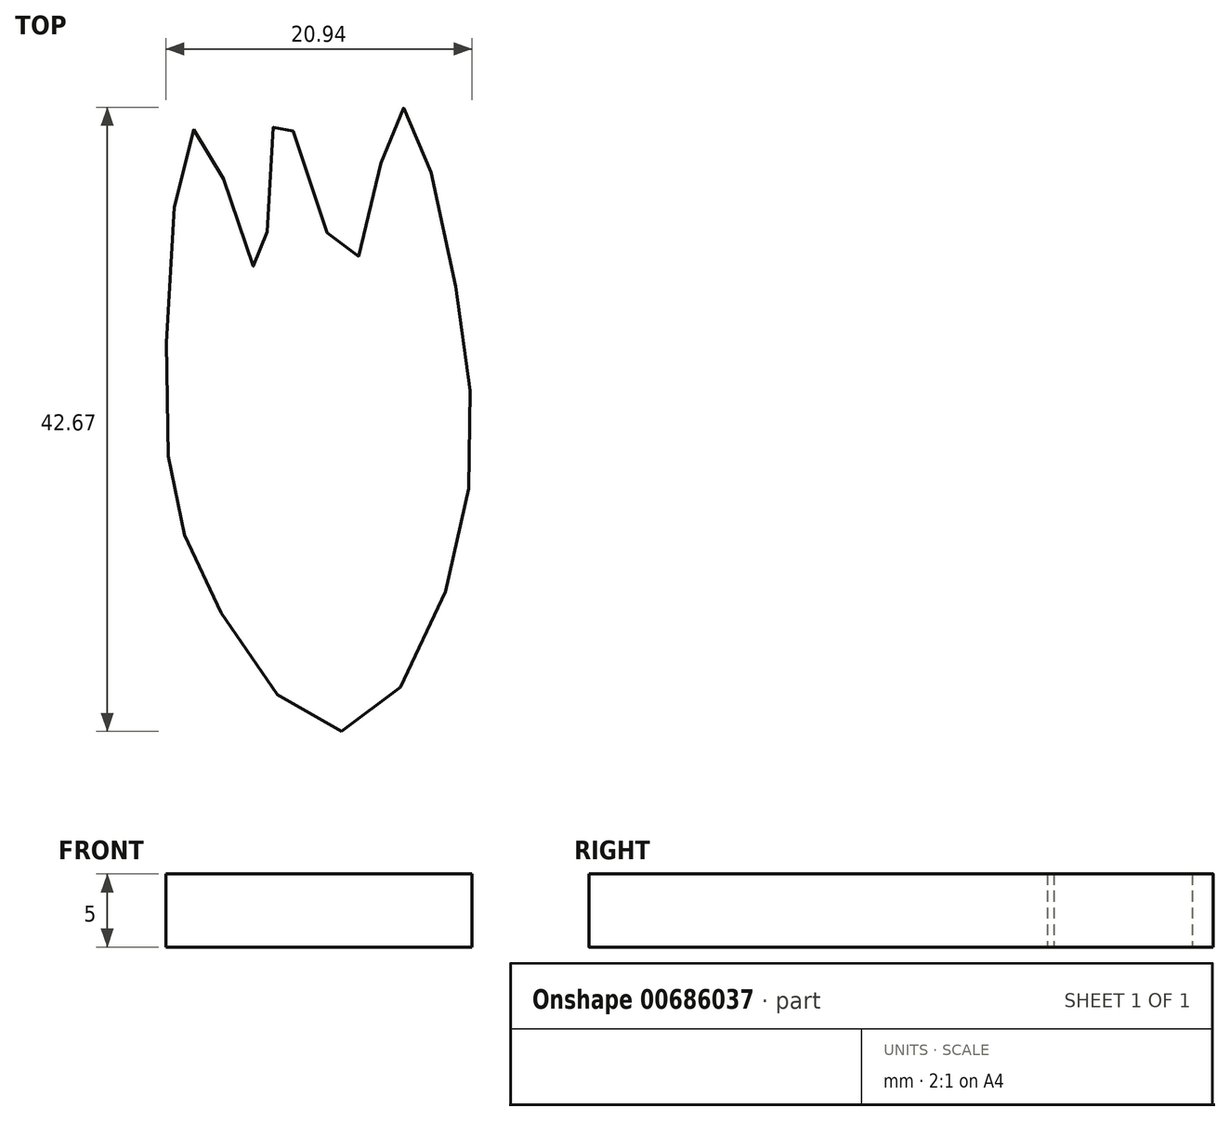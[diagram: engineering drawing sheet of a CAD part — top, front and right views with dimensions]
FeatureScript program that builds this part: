
annotation { "Feature Type Name" : "Feature", "Feature Type Description" : "" }
export const myFeature = defineFeature(function(context is Context, id is Id, definition is map)
    precondition{}
    {
        {
            var Q0;
            Q0=qCreatedBy(makeId("Top.planeOp"),FACE);
            var sketch = newSketch(context, id + "F0", { "sketchPlane" : qUnion([Q0])});
            skFitSpline(sketch, "E0", {"points": [v(31.23, -50.34) * mm, v(22.11, -40.56) * mm, v(19.22, -27) * mm, v(21.67, -9.22) * mm, v(25.67, -19) * mm, v(27, -7.67) * mm, v(31.67, -18.56) * mm, v(35, -7.89) * mm, v(38.78, -18.56) * mm, v(39.23, -37.67) * mm, v(31.23, -50.34) * mm]});
            skFitSpline(sketch, "E1", {"points": [v(11.06, -28.19) * mm, v(1.94, -18.4) * mm, v(-0.95, -4.85) * mm, v(1.5, 12.93) * mm, v(5.5, 3.15) * mm, v(6.83, 14.49) * mm, v(11.5, 3.6) * mm, v(14.83, 14.26) * mm, v(18.61, 3.6) * mm, v(19.06, -15.52) * mm, v(11.06, -28.19) * mm]});
            skSolve(sketch);
        }
        {
            var Q0;
            Q0=makeQuery(id+"F0.imprint","IMPRINT",FACE,{"disambiguationData":[TD([[makeQuery(id+"F0.imprint","IMPRINT",EDGE,{"derivedFrom":sQuery(id+"F0.wireOp",EDGE,"E0")}),-1.0]])]});
            extrude(context, id + "F1", {"entities" : qUnion([Q0]), "depth" : 5 * mm, "offsetDistance" : 25.4 * mm});
        }
    });
